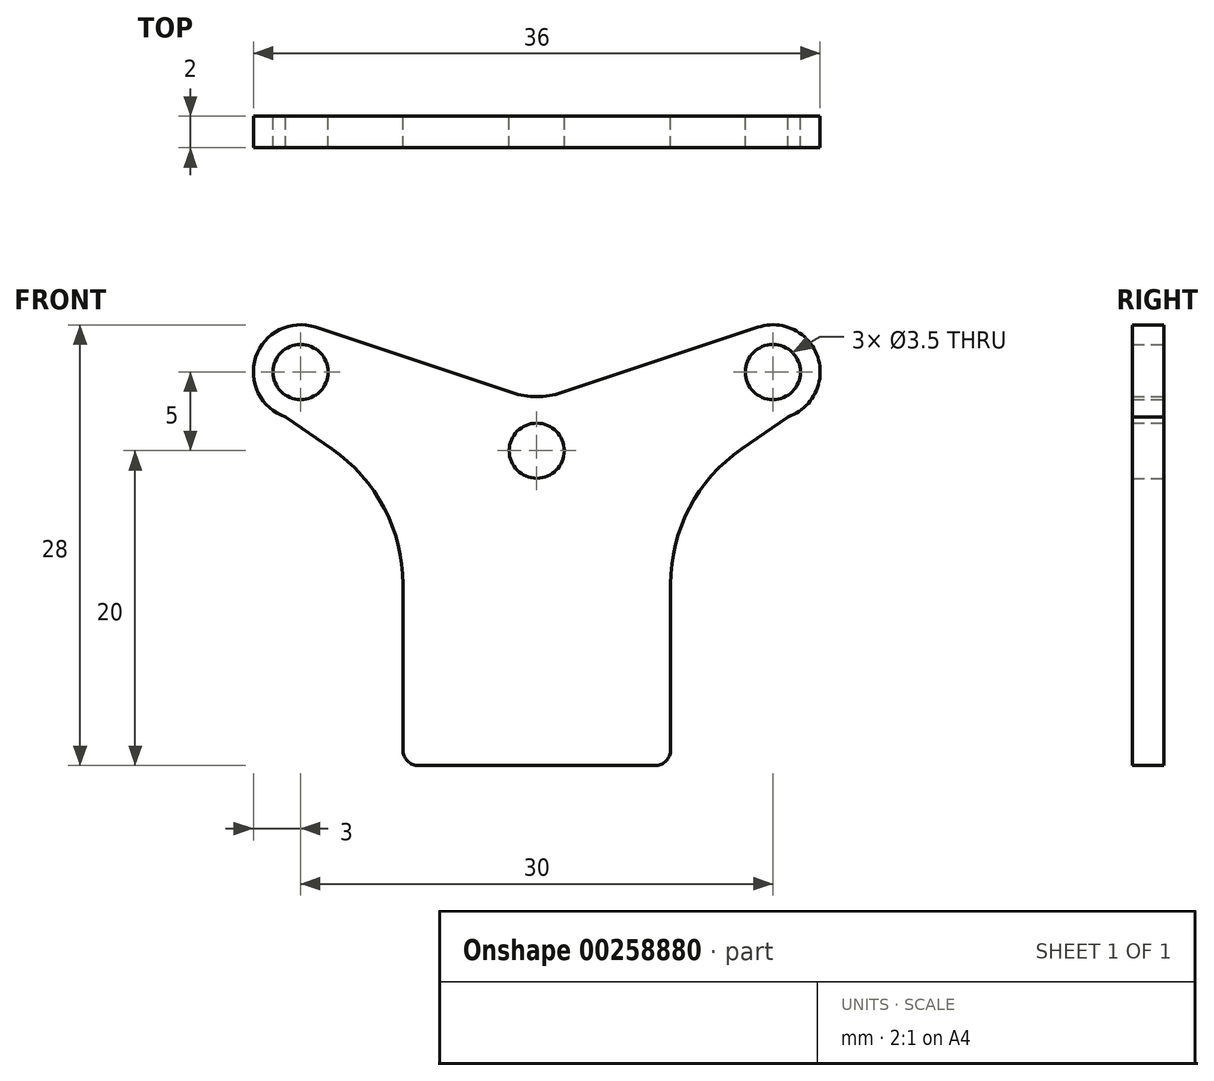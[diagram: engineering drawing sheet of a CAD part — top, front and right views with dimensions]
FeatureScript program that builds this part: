
annotation { "Feature Type Name" : "Feature", "Feature Type Description" : "" }
export const myFeature = defineFeature(function(context is Context, id is Id, definition is map)
    precondition{}
    {
        {
            var Q0;
            Q0=qCreatedBy(makeId("Front.planeOp"),FACE);
            var sketch = newSketch(context, id + "F0", { "sketchPlane" : qUnion([Q0])});
            skCircle(sketch, "E0", {"center": v(15, 0) * mm, "radius": 1.75 * mm});
            skCircle(sketch, "E1", {"center": v(0, -5) * mm, "radius": 1.75 * mm});
            skArc(sketch, "E2", {"start": v(15.95, -2.85) * mm, "mid": v(17.85, 0.95) * mm, "end": v(14.05, 2.85) * mm});
            skLineSegment(sketch, "E3", {"start": v(14.05, 2.85) * mm, "end": v(1.58, -1.31) * mm});
            skCircle(sketch, "E4.MirrorC", {"center": v(-15, 0) * mm, "radius": 1.75 * mm});
            skArc(sketch, "E5.MirrorC", {"start": v(-15.95, -2.85) * mm, "mid": v(-17.85, 0.95) * mm, "end": v(-14.05, 2.85) * mm});
            skLineSegment(sketch, "E6.MirrorCS", {"start": v(-14.05, 2.85) * mm, "end": v(-1.58, -1.31) * mm});
            skPoint(sketch, "E7.newPointA", {"position": v(0.95, -2.15) * mm});
            skPoint(sketch, "E7.newPointB", {"position": v(-0.95, -2.15) * mm});
            skArc(sketch, "E7.filletArc", {"start": v(-1.58, -1.31) * mm, "mid": v(0, -1.57) * mm, "end": v(1.58, -1.31) * mm});
            skLineSegment(sketch, "E8", {"start": v(8.5, -13.48) * mm, "end": v(8.5, -24) * mm});
            skLineSegment(sketch, "E9", {"start": v(7.5, -25) * mm, "end": v(0, -25) * mm});
            skLineSegment(sketch, "E10", {"start": v(13, -4.88) * mm, "end": v(15.95, -2.85) * mm});
            skPoint(sketch, "E11.visualSharp", {"position": v(8.5, -8) * mm});
            skArc(sketch, "E11.filletArc", {"start": v(13, -4.88) * mm, "mid": v(9.7, -8.63) * mm, "end": v(8.5, -13.48) * mm});
            skPoint(sketch, "E12.visualSharp", {"position": v(8.5, -25) * mm});
            skArc(sketch, "E12.filletArc", {"start": v(7.5, -25) * mm, "mid": v(8.2, -24.7) * mm, "end": v(8.5, -24) * mm});
            skArc(sketch, "E13.MirrorCS", {"start": v(-13, -4.88) * mm, "mid": v(-9.7, -8.63) * mm, "end": v(-8.5, -13.48) * mm});
            skLineSegment(sketch, "E14.MirrorCS", {"start": v(-13, -4.88) * mm, "end": v(-15.95, -2.85) * mm});
            skLineSegment(sketch, "E15.MirrorCS", {"start": v(-8.5, -13.48) * mm, "end": v(-8.5, -24) * mm});
            skLineSegment(sketch, "E16.MirrorCS", {"start": v(-7.5, -25) * mm, "end": v(0, -25) * mm});
            skPoint(sketch, "E17.MirrorP", {"position": v(-8.5, -25) * mm});
            skArc(sketch, "E18.MirrorCS", {"start": v(-7.5, -25) * mm, "mid": v(-8.2, -24.7) * mm, "end": v(-8.5, -24) * mm});
            skPoint(sketch, "E19.start.orphan", {"position": v(-0.95, -7.85) * mm});
            skPoint(sketch, "E20.start.orphan", {"position": v(0.95, -7.85) * mm});
            skSolve(sketch);
        }
        {
            var Q0;
            Q0=makeQuery(id+"F0.imprint","IMPRINT",FACE,{"disambiguationData":[TD([[makeQuery(id+"F0.imprint","IMPRINT",EDGE,{"derivedFrom":sQuery(id+"F0.wireOp",EDGE,"E0")}),-1.0]])]});
            extrude(context, id + "F1", {"entities" : qUnion([Q0]), "depth" : 2 * mm});
        }
    });
